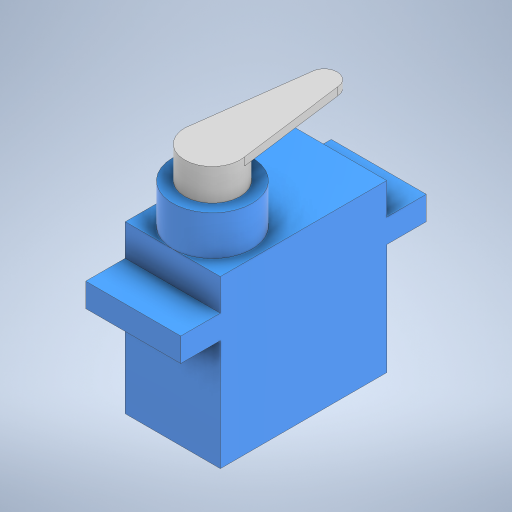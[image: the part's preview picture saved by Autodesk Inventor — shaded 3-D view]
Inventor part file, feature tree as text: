
AUTODESK INVENTOR PART (.ipt)
format: ipt  version: 2023 (Build 270158000, 158)  size: 303,616 bytes
history: native  units: mm
features: extrude x6, sketch x6, other x1
ambient origin geometry x8: Origin, YZ Plane, XZ Plane, XY Plane, X Axis, Y Axis, Z Axis, Center Point
bodies: Body1 (feature_tree)
feature tree (13):
  other  "Bryła1"
  extrude  "Wyciągnięcie proste1"  Depth=12.0mm
  extrude  "Wyciągnięcie proste2"  Depth=21.0mm
  extrude  "Wyciągnięcie proste3"  Depth=21.0mm TaperAngle=0.0deg
  extrude  "Wyciągnięcie proste4"  Depth=17.0mm
  extrude  "Wyciągnięcie proste5"  Depth=3.0mm
  extrude  "Wyciągnięcie proste6"  Depth=12.0mm
  sketch  "Szkic1"
  sketch  "Szkic2"
  sketch  "Szkic3"
  sketch  "Szkic4"
  sketch  "Szkic5"
  sketch  "Szkic6"
